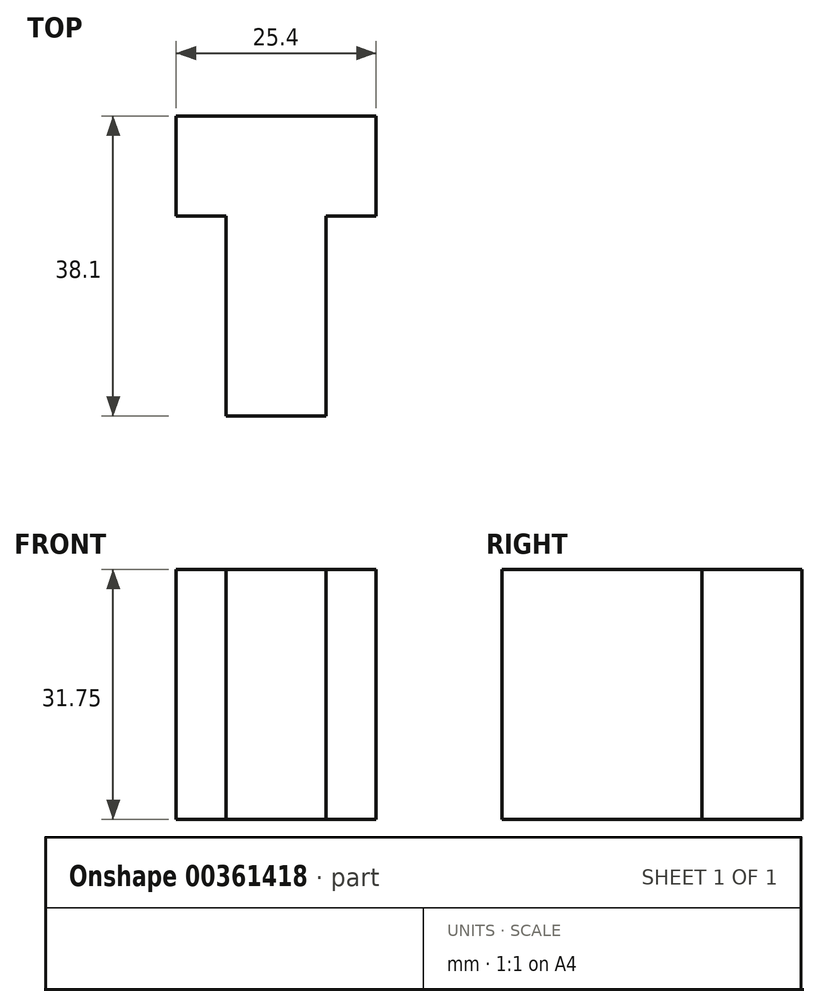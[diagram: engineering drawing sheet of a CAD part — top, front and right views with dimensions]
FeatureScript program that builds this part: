
annotation { "Feature Type Name" : "Feature", "Feature Type Description" : "" }
export const myFeature = defineFeature(function(context is Context, id is Id, definition is map)
    precondition{}
    {
        {
            var Q0;
            Q0=qCreatedBy(makeId("Top.planeOp"),FACE);
            var sketch = newSketch(context, id + "F0", { "sketchPlane" : qUnion([Q0])});
            skLineSegment(sketch, "E0", {"start": v(0, 0) * mm, "end": v(-6.35, 0) * mm});
            skLineSegment(sketch, "E1", {"start": v(-6.35, 0) * mm, "end": v(-6.35, 25.4) * mm});
            skLineSegment(sketch, "E2", {"start": v(-6.35, 25.4) * mm, "end": v(-12.7, 25.4) * mm});
            skLineSegment(sketch, "E3", {"start": v(-12.7, 25.4) * mm, "end": v(-12.7, 38.1) * mm});
            skLineSegment(sketch, "E4", {"start": v(-12.7, 38.1) * mm, "end": v(12.7, 38.1) * mm});
            skLineSegment(sketch, "E5", {"start": v(12.7, 38.1) * mm, "end": v(12.7, 25.4) * mm});
            skLineSegment(sketch, "E6", {"start": v(12.7, 25.4) * mm, "end": v(6.35, 25.4) * mm});
            skLineSegment(sketch, "E7", {"start": v(6.35, 25.4) * mm, "end": v(6.35, 0) * mm});
            skLineSegment(sketch, "E8", {"start": v(6.35, 0) * mm, "end": v(0, 0) * mm});
            skSolve(sketch);
        }
        {
            var Q0;
            Q0 = qSketchRegion(id + "F0", true);
            extrude(context, id + "F1", {"entities" : qUnion([Q0]), "depth" : 31.75 * mm});
        }
    });
